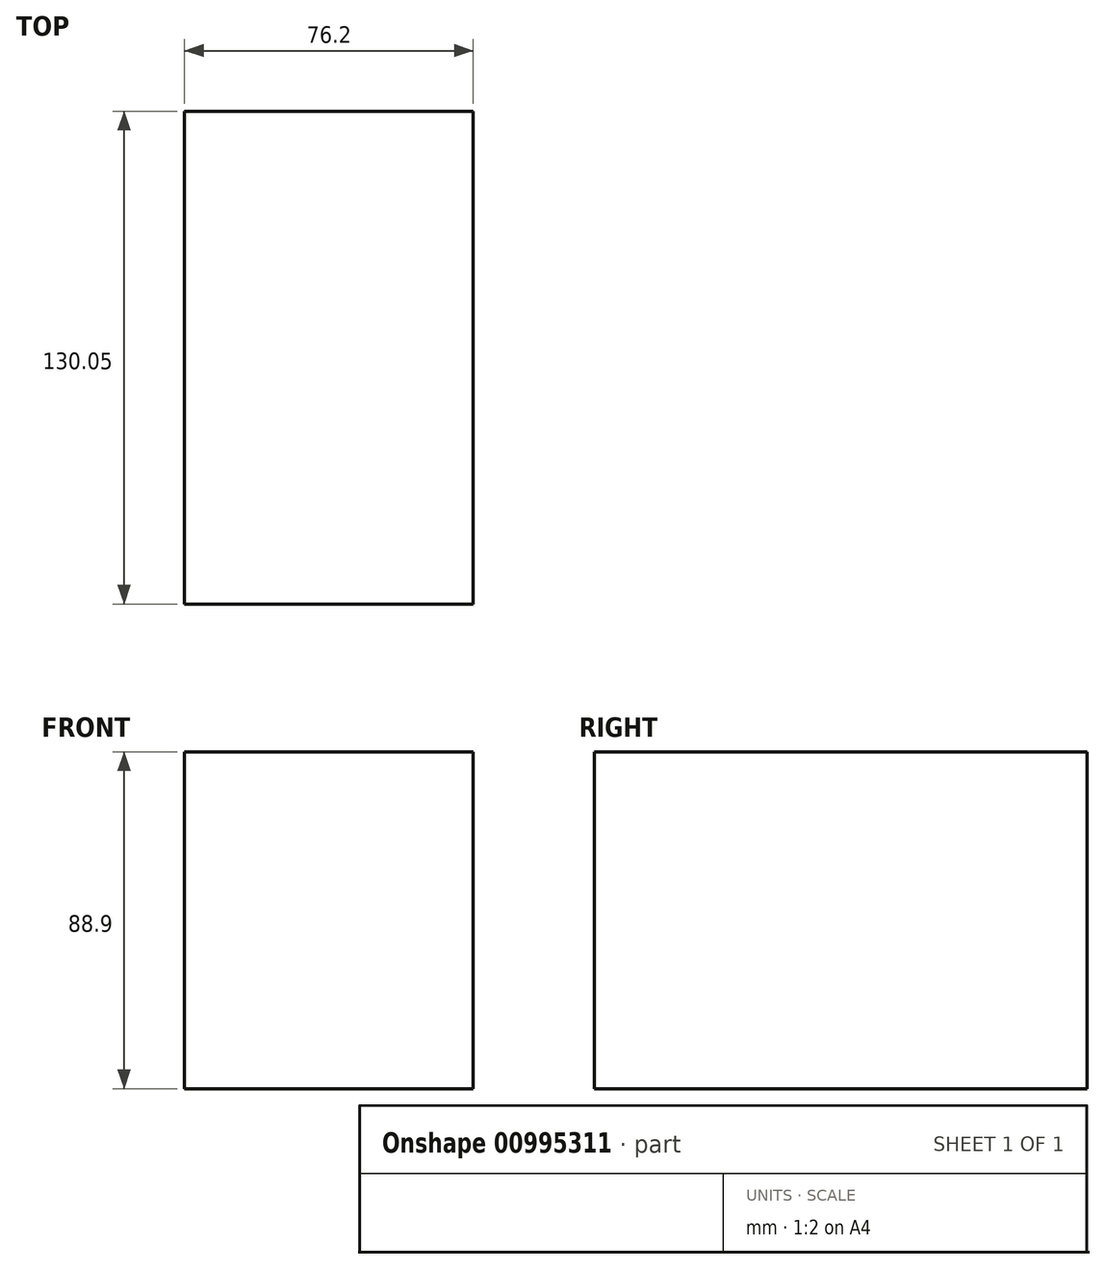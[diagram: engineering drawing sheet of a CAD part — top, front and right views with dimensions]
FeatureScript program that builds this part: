
annotation { "Feature Type Name" : "Feature", "Feature Type Description" : "" }
export const myFeature = defineFeature(function(context is Context, id is Id, definition is map)
    precondition{}
    {
        {
            var Q0;
            Q0=qCreatedBy(makeId("Front.planeOp"),FACE);
            var sketch = newSketch(context, id + "F0", { "sketchPlane" : qUnion([Q0])});
            skLineSegment(sketch, "E0.bottom", {"start": v(-38.1, 44.45) * mm, "end": v(38.1, 44.45) * mm});
            skLineSegment(sketch, "E0.top", {"start": v(-38.1, -44.45) * mm, "end": v(38.1, -44.45) * mm});
            skLineSegment(sketch, "E0.left", {"start": v(-38.1, 44.45) * mm, "end": v(-38.1, -44.45) * mm});
            skLineSegment(sketch, "E0.right", {"start": v(38.1, 44.45) * mm, "end": v(38.1, -44.45) * mm});
            skLineSegment(sketch, "E1", {"start": v(-38.1, 44.45) * mm, "end": v(38.1, -44.45) * mm, "construction": true});
            skPoint(sketch, "E2", {"position": v(0, 0) * mm});
            skSolve(sketch);
        }
        {
            var Q0;
            Q0=makeQuery(id+"F0.imprint","IMPRINT",FACE,{"disambiguationData":[TD([[makeQuery(id+"F0.imprint","IMPRINT",EDGE,{"derivedFrom":sQuery(id+"F0.wireOp",EDGE,"E0.bottom")}),-1.0]])]});
            extrude(context, id + "F1", {"entities" : qUnion([Q0]), "depth" : 130.05 * mm, "offsetDistance" : 25.4 * mm});
        }
    });
